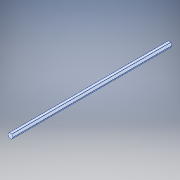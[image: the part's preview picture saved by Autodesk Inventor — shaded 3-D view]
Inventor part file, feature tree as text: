
AUTODESK INVENTOR PART (.ipt)
format: ipt  version: 2017 (Build 210142000, 142)  size: 107,008 bytes
history: native  units: in
note: dims shown in document units (in); Inventor stores cm internally (conversion verified against a paired STEP export)
features: fillet x1
ambient origin geometry x8: Origin, YZ Plane, XZ Plane, XY Plane, X Axis, Y Axis, Z Axis, Center Point
bodies: Solid1 (feature_tree)
feature tree (1):
  fillet  "Fillet1"  [1 undecoded]
note: 1 required parameter value undecoded (feature->parameter linkage not recoverable at this tier; creation-order binding heuristic only, values carry confidence <= 0.55)
